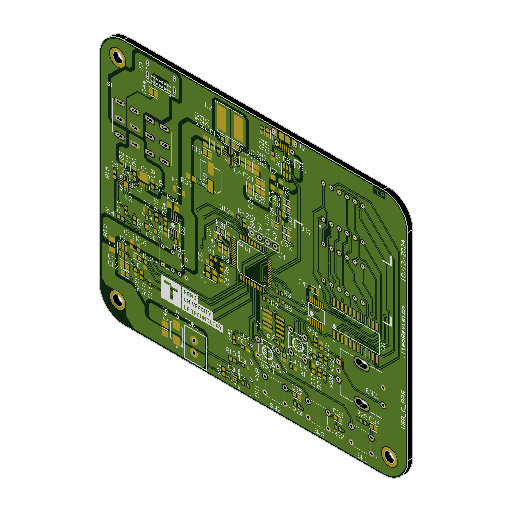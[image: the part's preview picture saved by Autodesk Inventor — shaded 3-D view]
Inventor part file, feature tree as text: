
AUTODESK INVENTOR PART (.ipt)
format: ipt  version: 2025 (Build 290162000, 162)  size: 2,297,344 bytes
history: native  units: in
note: dims shown in document units (in); Inventor stores cm internally (conversion verified against a paired STEP export)
features: sketch x127, hole x96, other x28, extrude x21
ambient origin geometry x8: Origin, YZ Plane, XZ Plane, XY Plane, X Axis, Y Axis, Z Axis, Center Point
bodies: Solid1 (feature_tree)
feature tree (272):
  other  "USB_C_PD_PPS_sink_BOARD"
  other  "BoardFrontPlane"
  extrude  "BoardOutline"  Depth=0.13in TaperAngle=0.0deg
  hole  "S2-4"  [1 undecoded]
  hole  "S2-3"  [1 undecoded]
  hole  "S2-2"  [1 undecoded]
  hole  "S2-1"  [1 undecoded]
  hole  "J4-1"  [1 undecoded]
  hole  "J4-4"  [1 undecoded]
  hole  "J4-3"  [1 undecoded]
  hole  "J4-2"  [1 undecoded]
  extrude  "S1-5"  Depth=0.13in TaperAngle=0.0deg
  extrude  "S1-2"  Depth=0.002in TaperAngle=0.0deg
  extrude  "S1-11"  Depth=0.002in TaperAngle=0.0deg
  extrude  "S1-8"  Depth=0.002in TaperAngle=0.0deg
  extrude  "S1-6"  Depth=0.002in TaperAngle=0.0deg
  extrude  "S1-3"  Depth=0.002in TaperAngle=0.0deg
  extrude  "S1-12"  [1 undecoded]
  extrude  "S1-9"  Depth=0.0472in TaperAngle=0.0deg
  extrude  "S1-7"  [1 undecoded]
  extrude  "S1-10"  [1 undecoded]
  extrude  "S1-1"  [1 undecoded]
  extrude  "S1-4"  [1 undecoded]
  hole  "K1-8"  [1 undecoded]
  hole  "K1-7"  [1 undecoded]
  hole  "K1-6"  [1 undecoded]
  hole  "K1-5"  [1 undecoded]
  hole  "K1-4"  [1 undecoded]
  hole  "K1-3"  [1 undecoded]
  hole  "K1-2"  [1 undecoded]
  hole  "K1-1"  [1 undecoded]
  extrude  "J3-3"  [1 undecoded]
  extrude  "J3-4"  [1 undecoded]
  extrude  "J3-1"  [1 undecoded]
  extrude  "J3-2"  [1 undecoded]
  hole  "J3-A1"  [1 undecoded]
  hole  "J3-A4"  [1 undecoded]
  hole  "J3-A5"  [1 undecoded]
  hole  "J3-A6"  [1 undecoded]
  hole  "J3-A7"  [1 undecoded]
  hole  "J3-A8"  [1 undecoded]
  hole  "J3-A9"  [1 undecoded]
  hole  "J3-A12"  [1 undecoded]
  hole  "J3-B1"  [1 undecoded]
  hole  "J3-B4"  [1 undecoded]
  hole  "J3-B5"  [1 undecoded]
  hole  "J3-B6"  [1 undecoded]
  hole  "J3-B7"  [1 undecoded]
  hole  "J3-B8"  [1 undecoded]
  hole  "J3-B9"  [1 undecoded]
  hole  "J3-B12"  [1 undecoded]
  hole  "J2-7"  [1 undecoded]
  hole  "J2-6"  [1 undecoded]
  extrude  "J2-11"  [1 undecoded]
  extrude  "J2-8"  [1 undecoded]
  hole  "ENC1-A"  [1 undecoded]
  hole  "ENC1-C"  [1 undecoded]
  hole  "ENC1-B"  [1 undecoded]
  extrude  "ENC1-3"  [1 undecoded]
  extrude  "ENC1-4"  [1 undecoded]
  hole  "ENC1-1"  [1 undecoded]
  hole  "ENC1-2"  [1 undecoded]
  hole  "DS2-7"  [1 undecoded]
  hole  "DS2-8"  [1 undecoded]
  hole  "DS2-9"  [1 undecoded]
  hole  "DS2-10"  [1 undecoded]
  hole  "DS2-11"  [1 undecoded]
  hole  "DS2-12"  [1 undecoded]
  hole  "DS2-1"  [1 undecoded]
  hole  "DS2-2"  [1 undecoded]
  hole  "DS2-3"  [1 undecoded]
  hole  "DS2-4"  [1 undecoded]
  hole  "DS2-5"  [1 undecoded]
  hole  "DS2-6"  [1 undecoded]
  hole  "DS1-7"  [1 undecoded]
  hole  "DS1-8"  [1 undecoded]
  hole  "DS1-9"  [1 undecoded]
  hole  "DS1-10"  [1 undecoded]
  hole  "DS1-11"  [1 undecoded]
  hole  "DS1-12"  [1 undecoded]
  hole  "DS1-1"  [1 undecoded]
  hole  "DS1-2"  [1 undecoded]
  hole  "DS1-3"  [1 undecoded]
  hole  "DS1-4"  [1 undecoded]
  hole  "DS1-5"  [1 undecoded]
  hole  "DS1-6"  [1 undecoded]
  hole  "Free-MH_UFFYUCRS"  [1 undecoded]
  hole  "Free-MH_NTYALDTJ"  [1 undecoded]
  hole  "Free-MH_SGBJWQGS"  [1 undecoded]
  other  "Decal_Top"
  other  "Decal_Bottom"
  hole  "LP3-TH_TUYHERHS"  [1 undecoded]
  hole  "LP3-TH_TUYHERHS_1"  [1 undecoded]
  hole  "LP3-TH_AGCPFLQI"  [1 undecoded]
  hole  "LP3-TH_AGCPFLQI_1"  [1 undecoded]
  hole  "LP2-TH_TJIVDCAF"  [1 undecoded]
  hole  "LP2-TH_TJIVDCAF_1"  [1 undecoded]
  hole  "LP2-TH_ARMWKDFP"  [1 undecoded]
  hole  "LP2-TH_ARMWKDFP_1"  [1 undecoded]
  hole  "LP1-TH_UMCDBLLX"  [1 undecoded]
  hole  "LP1-TH_UMCDBLLX_1"  [1 undecoded]
  hole  "LP1-TH_UEIXYMFC"  [1 undecoded]
  hole  "LP1-TH_UEIXYMFC_1"  [1 undecoded]
  hole  "S3-4"  [1 undecoded]
  hole  "S3-3"  [1 undecoded]
  hole  "S3-2"  [1 undecoded]
  hole  "S3-1"  [1 undecoded]
  hole  "SW3-4"  [1 undecoded]
  hole  "SW3-3"  [1 undecoded]
  hole  "SW3-2"  [1 undecoded]
  hole  "SW3-1"  [1 undecoded]
  hole  "SW2-1"  [1 undecoded]
  hole  "SW2-2"  [1 undecoded]
  hole  "SW2-3"  [1 undecoded]
  hole  "SW2-4"  [1 undecoded]
  hole  "SW1-4"  [1 undecoded]
  hole  "SW1-3"  [1 undecoded]
  hole  "SW1-2"  [1 undecoded]
  hole  "SW1-1"  [1 undecoded]
  hole  "CON1-1"  [1 undecoded]
  hole  "CON1-2"  [1 undecoded]
  sketch  "Sketch1"  dims[d0=0.0624in d1=0.0in]
  sketch  "Sketch14"  dims[d76=0.0394in d77=0.75in d78=0.375in d79=0.25in d80=0.5635in d81=1.0in d82=0.0in]
  sketch  "Sketch15"  dims[d83=0.0394in d84=0.75in d85=0.375in d86=0.25in d87=0.5635in d88=1.0in d89=0.0in]
  sketch  "Sketch16"  dims[d90=0.0394in d91=0.75in d92=0.375in d93=0.25in d94=0.5635in d95=1.0in d96=0.0in]
  sketch  "Sketch17"  dims[d97=0.0394in d98=0.75in d99=0.375in d100=0.25in d101=0.5635in d102=1.0in d103=0.0in]
  sketch  "Sketch18"  dims[d104=0.0402in d105=0.75in d106=0.375in d107=0.25in d108=0.5635in d109=1.0in d110=0.0in]
  sketch  "Sketch19"  dims[d111=0.0402in d112=0.75in d113=0.375in d114=0.25in d115=0.5635in d116=1.0in d117=0.0in]
  sketch  "Sketch20"  dims[d118=0.0402in d119=0.75in d120=0.375in d121=0.25in d122=0.5635in d123=1.0in d124=0.0in]
  sketch  "Sketch21"  dims[d125=0.0402in d126=0.75in d127=0.375in d128=0.25in d129=0.5635in d130=1.0in d131=0.0in d216=0.13in d217=0.0in]
  sketch  "Sketch34"  dims[d218=0.13in d219=0.0in d220=0.13in d221=0.0in]
  sketch  "Sketch35"  dims[d222=0.13in d223=0.0in d224=0.13in d225=0.0in]
  sketch  "Sketch36"  dims[d226=0.13in d227=0.0in d228=0.13in d229=0.0in]
  sketch  "Sketch37"  dims[d230=0.13in d231=0.0in d232=0.13in d233=0.0in]
  sketch  "Sketch38"  dims[d234=0.13in d235=0.0in d236=0.13in d237=0.0in]
  sketch  "Sketch39"  dims[d238=0.13in d239=0.0in]
  sketch  "Sketch40"  dims[d240=0.0315in d241=0.75in d242=0.375in d243=0.25in d244=0.5635in d245=1.0in d246=0.0in]
  sketch  "Sketch41"  dims[d247=0.0315in d248=0.75in d249=0.375in d250=0.25in d251=0.5635in d252=1.0in d253=0.0in]
  sketch  "Sketch42"  dims[d254=0.0315in d255=0.75in d256=0.375in d257=0.25in d258=0.5635in d259=1.0in d260=0.0in]
  sketch  "Sketch43"  dims[d261=0.0315in d262=0.75in d263=0.375in d264=0.25in d265=0.5635in d266=1.0in d267=0.0in]
  sketch  "Sketch44"  dims[d268=0.0315in d269=0.75in d270=0.375in d271=0.25in d272=0.5635in d273=1.0in d274=0.0in]
  sketch  "Sketch45"  dims[d275=0.0315in d276=0.75in d277=0.375in d278=0.25in d279=0.5635in d280=1.0in d281=0.0in]
  sketch  "Sketch46"  dims[d282=0.0315in d283=0.75in d284=0.375in d285=0.25in d286=0.5635in d287=1.0in d288=0.0in]
  sketch  "Sketch47"  dims[d289=0.0315in d290=0.75in d291=0.375in d292=0.25in d293=0.5635in d294=1.0in d295=0.0in d296=0.13in d297=0.0in]
  sketch  "Sketch48"  dims[d298=0.13in d299=0.0in d300=0.13in d301=0.0in]
  sketch  "Sketch49"  dims[d302=0.13in d303=0.0in]
  sketch  "Sketch50"  dims[d304=0.0157in d305=0.75in d306=0.375in d307=0.25in d308=0.5635in d309=1.0in d310=0.0in]
  sketch  "Sketch51"  dims[d311=0.0157in d312=0.75in d313=0.375in d314=0.25in d315=0.5635in d316=1.0in d317=0.0in]
  sketch  "Sketch52"  dims[d318=0.0157in d319=0.75in d320=0.375in d321=0.25in d322=0.5635in d323=1.0in d324=0.0in]
  sketch  "Sketch53"  dims[d325=0.0157in d326=0.75in d327=0.375in d328=0.25in d329=0.5635in d330=1.0in d331=0.0in]
  sketch  "Sketch54"  dims[d332=0.0157in d333=0.75in d334=0.375in d335=0.25in d336=0.5635in d337=1.0in d338=0.0in]
  sketch  "Sketch55"  dims[d339=0.0157in d340=0.75in d341=0.375in d342=0.25in d343=0.5635in d344=1.0in d345=0.0in]
  sketch  "Sketch56"  dims[d346=0.0157in d347=0.75in d348=0.375in d349=0.25in d350=0.5635in d351=1.0in d352=0.0in]
  sketch  "Sketch57"  dims[d353=0.0157in d354=0.75in d355=0.375in d356=0.25in d357=0.5635in d358=1.0in d359=0.0in]
  sketch  "Sketch58"  dims[d360=0.0157in d361=0.75in d362=0.375in d363=0.25in d364=0.5635in d365=1.0in d366=0.0in]
  sketch  "Sketch59"  dims[d367=0.0157in d368=0.75in d369=0.375in d370=0.25in d371=0.5635in d372=1.0in d373=0.0in]
  sketch  "Sketch60"  dims[d374=0.0157in d375=0.75in d376=0.375in d377=0.25in d378=0.5635in d379=1.0in d380=0.0in]
  sketch  "Sketch61"  dims[d381=0.0157in d382=0.75in d383=0.375in d384=0.25in d385=0.5635in d386=1.0in d387=0.0in]
  sketch  "Sketch62"  dims[d388=0.0157in d389=0.75in d390=0.375in d391=0.25in d392=0.5635in d393=1.0in d394=0.0in]
  sketch  "Sketch63"  dims[d395=0.0157in d396=0.75in d397=0.375in d398=0.25in d399=0.5635in d400=1.0in d401=0.0in]
  sketch  "Sketch64"  dims[d402=0.0157in d403=0.75in d404=0.375in d405=0.25in d406=0.5635in d407=1.0in d408=0.0in]
  sketch  "Sketch65"  dims[d409=0.0157in d410=0.75in d411=0.375in d412=0.25in d413=0.5635in d414=1.0in d415=0.0in]
  sketch  "Sketch66"  dims[d416=0.0335in d417=0.75in d418=0.375in d419=0.25in d420=0.5635in d421=1.0in d422=0.0in]
  sketch  "Sketch67"  dims[d423=0.0335in d424=0.75in d425=0.375in d426=0.25in d427=0.5635in d428=1.0in d429=0.0in d430=0.13in d431=0.0in]
  sketch  "Sketch68"  dims[d432=0.13in d433=0.0in]
  sketch  "Sketch69"  dims[d434=0.0394in d435=0.75in d436=0.375in d437=0.25in d438=0.5635in d439=1.0in d440=0.0in]
  sketch  "Sketch70"  dims[d441=0.0394in d442=0.75in d443=0.375in d444=0.25in d445=0.5635in d446=1.0in d447=0.0in]
  sketch  "Sketch71"  dims[d448=0.0394in d449=0.75in d450=0.375in d451=0.25in d452=0.5635in d453=1.0in d454=0.0in d455=0.13in d456=0.0in]
  sketch  "Sketch72"  dims[d457=0.13in d458=0.0in]
  sketch  "Sketch73"  dims[d459=0.0394in d460=0.75in d461=0.375in d462=0.25in d463=0.5635in d464=1.0in d465=0.0in]
  sketch  "Sketch74"  dims[d466=0.0394in d467=0.75in d468=0.375in d469=0.25in d470=0.5635in d471=1.0in d472=0.0in]
  sketch  "Sketch75"  dims[d473=0.0295in d474=0.75in d475=0.375in d476=0.25in d477=0.5635in d478=1.0in d479=0.0in]
  sketch  "Sketch76"  dims[d480=0.0295in d481=0.75in d482=0.375in d483=0.25in d484=0.5635in d485=1.0in d486=0.0in]
  sketch  "Sketch77"  dims[d487=0.0295in d488=0.75in d489=0.375in d490=0.25in d491=0.5635in d492=1.0in d493=0.0in]
  sketch  "Sketch78"  dims[d494=0.0295in d495=0.75in d496=0.375in d497=0.25in d498=0.5635in d499=1.0in d500=0.0in]
  sketch  "Sketch79"  dims[d501=0.0295in d502=0.75in d503=0.375in d504=0.25in d505=0.5635in d506=1.0in d507=0.0in]
  sketch  "Sketch80"  dims[d508=0.0295in d509=0.75in d510=0.375in d511=0.25in d512=0.5635in d513=1.0in d514=0.0in]
  sketch  "Sketch81"  dims[d515=0.0295in d516=0.75in d517=0.375in d518=0.25in d519=0.5635in d520=1.0in d521=0.0in]
  sketch  "Sketch82"  dims[d522=0.0295in d523=0.75in d524=0.375in d525=0.25in d526=0.5635in d527=1.0in d528=0.0in]
  sketch  "Sketch83"  dims[d529=0.0295in d530=0.75in d531=0.375in d532=0.25in d533=0.5635in d534=1.0in d535=0.0in]
  sketch  "Sketch84"  dims[d536=0.0295in d537=0.75in d538=0.375in d539=0.25in d540=0.5635in d541=1.0in d542=0.0in]
  sketch  "Sketch85"  dims[d543=0.0295in d544=0.75in d545=0.375in d546=0.25in d547=0.5635in d548=1.0in d549=0.0in]
  sketch  "Sketch86"  dims[d550=0.0295in d551=0.75in d552=0.375in d553=0.25in d554=0.5635in d555=1.0in d556=0.0in]
  sketch  "Sketch87"  dims[d557=0.0295in d558=0.75in d559=0.375in d560=0.25in d561=0.5635in d562=1.0in d563=0.0in]
  sketch  "Sketch88"  dims[d564=0.0295in d565=0.75in d566=0.375in d567=0.25in d568=0.5635in d569=1.0in d570=0.0in]
  sketch  "Sketch89"  dims[d571=0.0295in d572=0.75in d573=0.375in d574=0.25in d575=0.5635in d576=1.0in d577=0.0in]
  sketch  "Sketch90"  dims[d578=0.0295in d579=0.75in d580=0.375in d581=0.25in d582=0.5635in d583=1.0in d584=0.0in]
  sketch  "Sketch91"  dims[d585=0.0295in d586=0.75in d587=0.375in d588=0.25in d589=0.5635in d590=1.0in d591=0.0in]
  sketch  "Sketch92"  dims[d592=0.0295in d593=0.75in d594=0.375in d595=0.25in d596=0.5635in d597=1.0in d598=0.0in]
  sketch  "Sketch93"  dims[d599=0.0295in d600=0.75in d601=0.375in d602=0.25in d603=0.5635in d604=1.0in d605=0.0in]
  sketch  "Sketch94"  dims[d606=0.0295in d607=0.75in d608=0.375in d609=0.25in d610=0.5635in d611=1.0in d612=0.0in]
  sketch  "Sketch95"  dims[d613=0.0295in d614=0.75in d615=0.375in d616=0.25in d617=0.5635in d618=1.0in d619=0.0in]
  sketch  "Sketch96"  dims[d620=0.0295in d621=0.75in d622=0.375in d623=0.25in d624=0.5635in d625=1.0in d626=0.0in]
  sketch  "Sketch97"  dims[d627=0.0295in d628=0.75in d629=0.375in d630=0.25in d631=0.5635in d632=1.0in d633=0.0in]
  sketch  "Sketch98"  dims[d634=0.0295in d635=0.75in d636=0.375in d637=0.25in d638=0.5635in d639=1.0in d640=0.0in]
  sketch  "Sketch99"  dims[d655=0.126in d656=0.75in d657=0.375in d658=0.25in d659=0.5635in d660=1.0in d661=0.0in]
  sketch  "Sketch100"  dims[d662=0.126in d663=0.75in d664=0.375in d665=0.25in d666=0.5635in d667=1.0in d668=0.0in]
  sketch  "Sketch101"  dims[d669=0.126in d670=0.75in d671=0.375in d672=0.25in d673=0.5635in d674=1.0in d675=0.0in d678=0.002in d679=0.0in]
  sketch  "Sketch102"  dims[d680=0.002in d681=0.0in d682=0.002in d683=0.0in]
  sketch  "Sketch103"  dims[d684=0.002in d685=0.0in d686=0.002in d687=0.0in]
  sketch  "Sketch104"  dims[d688=0.002in d689=0.0in d690=0.002in d691=0.0in]
  sketch  "Sketch105"  dims[d692=0.002in d693=0.0in d694=0.002in d695=0.0in]
  sketch  "Sketch106"  dims[d696=0.0624in d698=-0.0624in]
  sketch  "Sketch107"  dims[d700=0.0244in d701=0.75in d702=0.375in d703=0.25in d704=0.5635in d705=1.0in d706=0.0in]
  sketch  "Sketch108"  dims[d707=0.0244in d708=0.75in d709=0.375in d710=0.25in d711=0.5635in d712=1.0in d713=0.0in]
  sketch  "Sketch111"  dims[d714=0.0244in d715=0.75in d716=0.375in d717=0.25in d718=0.5635in d719=1.0in d720=0.0in]
  sketch  "Sketch112"  dims[d721=0.0244in d722=0.75in d723=0.375in d724=0.25in d725=0.5635in d726=1.0in d727=0.0in]
  sketch  "Sketch113"  dims[d728=0.0244in d729=0.75in d730=0.375in d731=0.25in d732=0.5635in d733=1.0in d734=0.0in]
  sketch  "Sketch115"  dims[d735=0.0244in d736=0.75in d737=0.375in d738=0.25in d739=0.5635in d740=1.0in d741=0.0in]
  other  "Srf2"
  sketch  "Sketch116"  dims[d742=0.0244in d743=0.75in d744=0.375in d745=0.25in d746=0.5635in d747=1.0in d748=0.0in]
  other  "Srf3"
  sketch  "Sketch117"  dims[d749=0.0244in d750=0.75in d751=0.375in d752=0.25in d753=0.5635in d754=1.0in d755=0.0in]
  other  "Srf4"
  sketch  "Sketch118"  dims[d756=0.0244in d757=0.75in d758=0.375in d759=0.25in d760=0.5635in d761=1.0in d762=0.0in]
  other  "Srf5"
  sketch  "Sketch119"  dims[d763=0.0244in d764=0.75in d765=0.375in d766=0.25in d767=0.5635in d768=1.0in d769=0.0in]
  other  "Srf6"
  sketch  "Sketch120"  dims[d770=0.0244in d771=0.75in d772=0.375in d773=0.25in d774=0.5635in d775=1.0in d776=0.0in]
  other  "Srf7"
  sketch  "Sketch121"  dims[d777=0.0244in d778=0.75in d779=0.375in d780=0.25in d781=0.5635in d782=1.0in d783=0.0in]
  other  "Srf8"
  sketch  "Sketch122"  dims[d784=0.0394in d785=0.75in d786=0.375in d787=0.25in d788=0.5635in d789=1.0in d790=0.0in]
  other  "Srf9"
  sketch  "Sketch123"  dims[d791=0.0394in d792=0.75in d793=0.375in d794=0.25in d795=0.5635in d796=1.0in d797=0.0in]
  other  "Srf10"
  other  "img_Top"
  other  "G_1340010729_TopDecalImage"
  other  "img_Bottom"
  other  "G_1340010729_BottomDecalImage"
  sketch  "Sketch126"  dims[d798=0.0394in d799=0.75in d800=0.375in d801=0.25in d802=0.5635in d803=1.0in d804=0.0in]
  sketch  "Sketch127"  dims[d805=0.0394in d806=0.75in d807=0.375in d808=0.25in d809=0.5635in d810=1.0in d811=0.0in]
  sketch  "Sketch128"  dims[d812=0.0413in d813=0.75in d814=0.375in d815=0.25in d816=0.5635in d817=1.0in d818=0.0in]
  sketch  "Sketch129"  dims[d819=0.0413in d820=0.75in d821=0.375in d822=0.25in d823=0.5635in d824=1.0in d825=0.0in]
  sketch  "Sketch130"  dims[d826=0.0413in d827=0.75in d828=0.375in d829=0.25in d830=0.5635in d831=1.0in d832=0.0in]
  sketch  "Sketch131"  dims[d833=0.0413in d834=0.75in d835=0.375in d836=0.25in d837=0.5635in d838=1.0in d839=0.0in]
  sketch  "Sketch132"  dims[d840=0.0413in d841=0.75in d842=0.375in d843=0.25in d844=0.5635in d845=1.0in d846=0.0in]
  sketch  "Sketch133"  dims[d847=0.0413in d848=0.75in d849=0.375in d850=0.25in d851=0.5635in d852=1.0in d853=0.0in]
  sketch  "Sketch134"  dims[d854=0.0413in d855=0.75in d856=0.375in d857=0.25in d858=0.5635in d859=1.0in d860=0.0in]
  sketch  "Sketch135"  dims[d861=0.0413in d862=0.75in d863=0.375in d864=0.25in d865=0.5635in d866=1.0in d867=0.0in]
  sketch  "Sketch136"  dims[d868=0.0413in d869=0.75in d870=0.375in d871=0.25in d872=0.5635in d873=1.0in d874=0.0in]
  sketch  "Sketch137"  dims[d875=0.0413in d876=0.75in d877=0.375in d878=0.25in d879=0.5635in d880=1.0in d881=0.0in]
  sketch  "Sketch138"  dims[d882=0.0413in d883=0.75in d884=0.375in d885=0.25in d886=0.5635in d887=1.0in d888=0.0in]
  sketch  "Sketch139"  dims[d889=0.0413in d890=0.75in d891=0.375in d892=0.25in d893=0.5635in d894=1.0in d895=0.0in]
  sketch  "Sketch140"  dims[d896=0.0472in d897=0.75in d898=0.375in d899=0.25in d900=0.5635in d901=1.0in d902=0.0in]
  sketch  "Sketch141"  dims[d903=0.0472in d904=0.75in d905=0.375in d906=0.25in d907=0.5635in d908=1.0in d909=0.0in d910=0.002in d911=0.0in]
  sketch  "Sketch142"
  sketch  "Sketch143"
  sketch  "Sketch144"
  sketch  "Sketch145"
  sketch  "Sketch146"
  sketch  "Sketch147"
  sketch  "Sketch148"
  sketch  "Sketch149"
  sketch  "Sketch150"
  sketch  "Sketch151"
  sketch  "Sketch152"
  sketch  "Sketch153"
  sketch  "Sketch154"
  sketch  "Sketch155"
  sketch  "Sketch156"
  other  "Srf11"
  other  "UI_BTNs"
  other  "U_Buck_boost"
  other  "MCU"
  other  "LOAD_SENSE"
  other  "Protection"
  other  "USB_B"
  other  "LDO"
  other  "Encoder"
  other  "OCP"
  other  "RoomDefinition"
note: 109 required parameter values undecoded (feature->parameter linkage not recoverable at this tier; creation-order binding heuristic only, values carry confidence <= 0.55)
